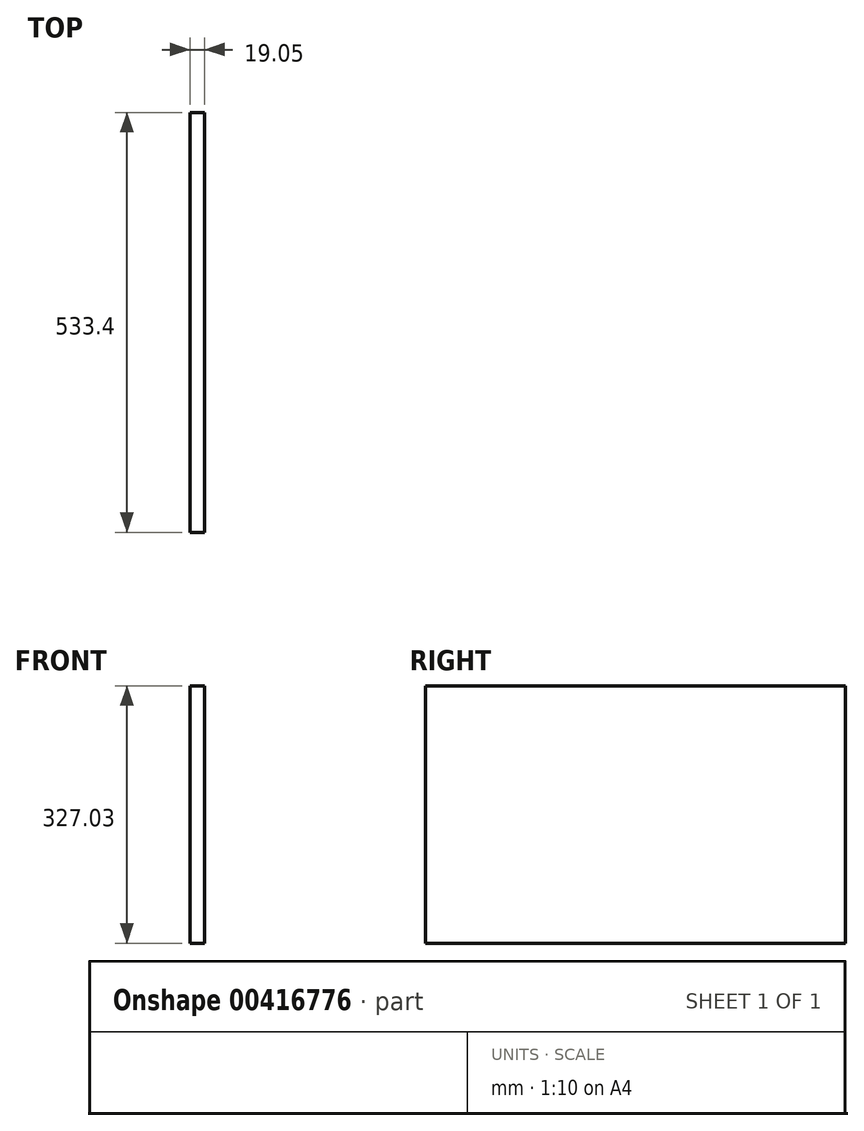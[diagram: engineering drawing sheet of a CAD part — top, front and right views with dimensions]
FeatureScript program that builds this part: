
annotation { "Feature Type Name" : "Feature", "Feature Type Description" : "" }
export const myFeature = defineFeature(function(context is Context, id is Id, definition is map)
    precondition{}
    {
        {
            var Q0;
            Q0=qCreatedBy(makeId("Right.planeOp"),FACE);
            var sketch = newSketch(context, id + "F0", { "sketchPlane" : qUnion([Q0])});
            skLineSegment(sketch, "E0.bottom", {"start": v(0, 0) * mm, "end": v(533.4, 0) * mm});
            skLineSegment(sketch, "E0.top", {"start": v(0, 327.02) * mm, "end": v(533.4, 327.02) * mm});
            skLineSegment(sketch, "E0.left", {"start": v(0, 0) * mm, "end": v(0, 327.02) * mm});
            skLineSegment(sketch, "E0.right", {"start": v(533.4, 0) * mm, "end": v(533.4, 327.02) * mm});
            skSolve(sketch);
        }
        {
            var Q0;
            Q0 = qSketchRegion(id + "F0", true);
            extrude(context, id + "F1", {"entities" : qUnion([Q0]), "depth" : 19.05 * mm});
        }
    });
